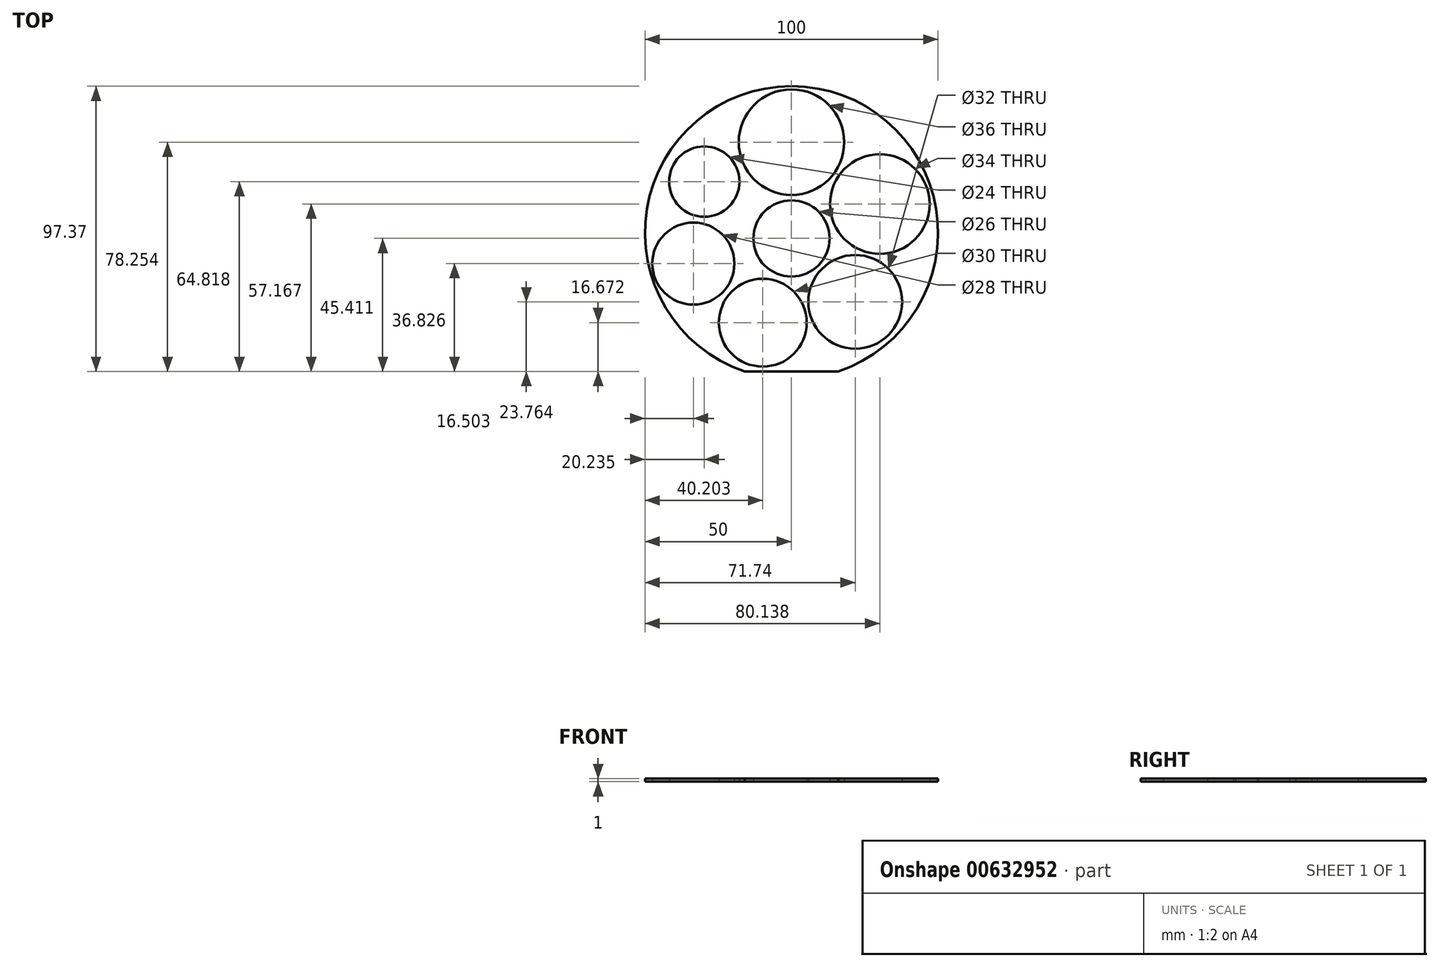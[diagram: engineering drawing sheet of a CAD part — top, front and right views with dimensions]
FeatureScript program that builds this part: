
annotation { "Feature Type Name" : "Feature", "Feature Type Description" : "" }
export const myFeature = defineFeature(function(context is Context, id is Id, definition is map)
    precondition{}
    {
        {
            var Q0;
            Q0=qCreatedBy(makeId("Top.planeOp"),FACE);
            var sketch = newSketch(context, id + "F0", { "sketchPlane" : qUnion([Q0])});
            skArc(sketch, "E0", {"start": v(16, -47.37) * mm, "mid": v(0, 50) * mm, "end": v(-16, -47.37) * mm});
            skLineSegment(sketch, "E1", {"start": v(-16, -47.37) * mm, "end": v(16, -47.37) * mm});
            skCircle(sketch, "E2", {"center": v(21.74, -23.6) * mm, "radius": 16 * mm});
            skCircle(sketch, "E3", {"center": v(0, 30.88) * mm, "radius": 18 * mm});
            skCircle(sketch, "E4", {"center": v(30.14, 9.8) * mm, "radius": 17 * mm});
            skCircle(sketch, "E5", {"center": v(-29.76, 17.45) * mm, "radius": 12 * mm});
            skCircle(sketch, "E6", {"center": v(0, -1.96) * mm, "radius": 13 * mm});
            skCircle(sketch, "E7", {"center": v(-9.8, -30.7) * mm, "radius": 15 * mm});
            skCircle(sketch, "E8", {"center": v(-33.5, -10.54) * mm, "radius": 14 * mm});
            skSolve(sketch);
        }
        {
            var Q0;
            Q0=makeQuery(id+"F0.imprint","IMPRINT",FACE,{"disambiguationData":[TD([[makeQuery(id+"F0.imprint","IMPRINT",EDGE,{"derivedFrom":sQuery(id+"F0.wireOp",EDGE,"E0")}),1.0]])]});
            extrude(context, id + "F1", {"entities" : qUnion([Q0]), "depth" : 1 * mm, "offsetDistance" : 25 * mm});
        }
    });
